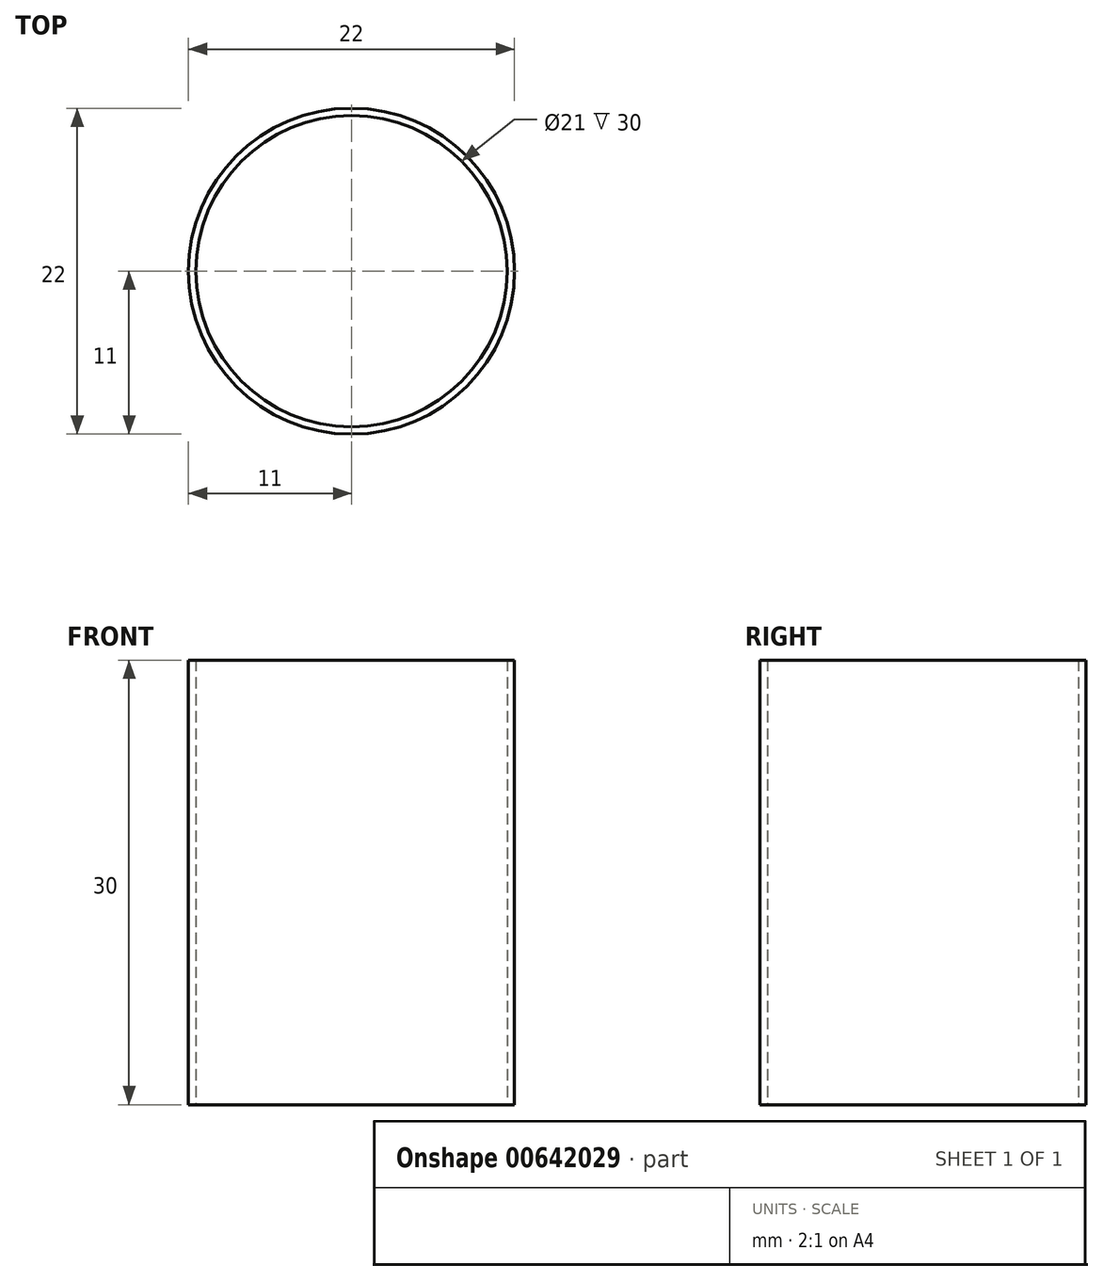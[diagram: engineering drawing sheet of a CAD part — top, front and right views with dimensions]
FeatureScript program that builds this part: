
annotation { "Feature Type Name" : "Feature", "Feature Type Description" : "" }
export const myFeature = defineFeature(function(context is Context, id is Id, definition is map)
    precondition{}
    {
        {
            var Q0;
            Q0=qCreatedBy(makeId("Top.planeOp"),FACE);
            var sketch = newSketch(context, id + "F0", { "sketchPlane" : qUnion([Q0])});
            skCircle(sketch, "E0", {"center": v(0, 0) * mm, "radius": 11 * mm});
            skCircle(sketch, "E1", {"center": v(0, 0) * mm, "radius": 10.5 * mm});
            skSolve(sketch);
        }
        {
            var Q0;
            Q0=makeQuery(id+"F0.imprint","IMPRINT",FACE,{"disambiguationData":[TD([[makeQuery(id+"F0.imprint","IMPRINT",EDGE,{"derivedFrom":sQuery(id+"F0.wireOp",EDGE,"E0")}),1.0]])]});
            extrude(context, id + "F1", {"entities" : qUnion([Q0]), "depth" : 30 * mm, "offsetDistance" : 25 * mm});
        }
    });
